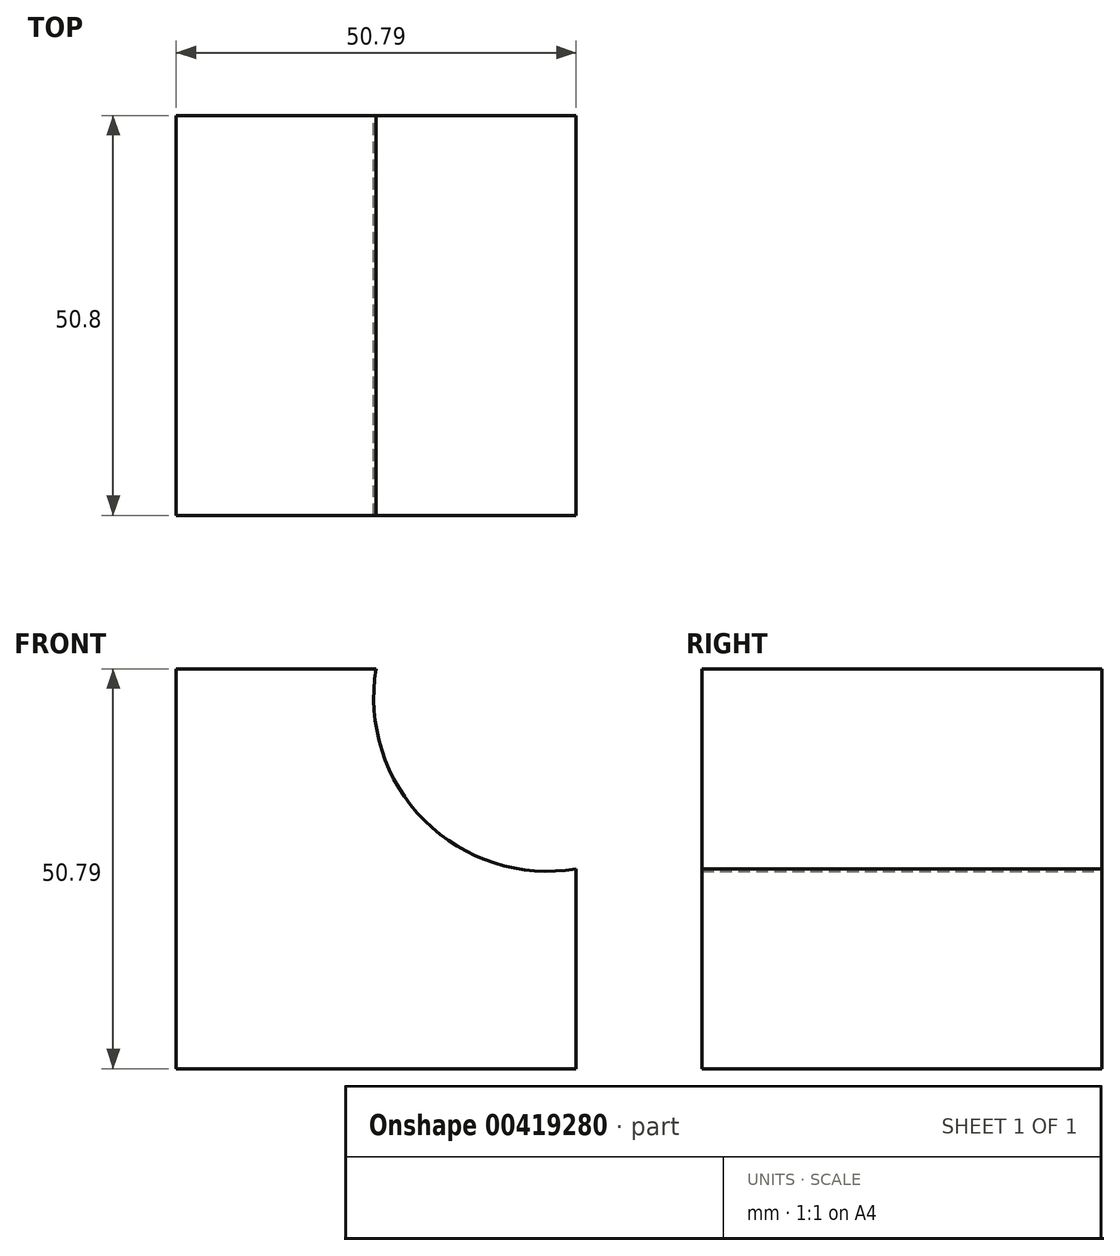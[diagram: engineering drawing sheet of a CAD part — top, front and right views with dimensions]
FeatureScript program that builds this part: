
annotation { "Feature Type Name" : "Feature", "Feature Type Description" : "" }
export const myFeature = defineFeature(function(context is Context, id is Id, definition is map)
    precondition{}
    {
        {
            var Q0;
            Q0=qCreatedBy(makeId("Front.planeOp"),FACE);
            var sketch = newSketch(context, id + "F0", { "sketchPlane" : qUnion([Q0])});
            skLineSegment(sketch, "E0", {"start": v(0, 0) * mm, "end": v(0, 50.8) * mm});
            skLineSegment(sketch, "E1", {"start": v(0, 50.8) * mm, "end": v(25.4, 50.8) * mm});
            skLineSegment(sketch, "E2", {"start": v(0, 0) * mm, "end": v(50.8, 0) * mm});
            skLineSegment(sketch, "E3", {"start": v(50.8, 0) * mm, "end": v(50.8, 25.4) * mm});
            skArc(sketch, "E4", {"start": v(25.4, 50.8) * mm, "mid": v(31.53, 31.53) * mm, "end": v(50.8, 25.4) * mm});
            skSolve(sketch);
        }
        {
            var Q0;
            Q0=makeQuery(id+"F0.imprint","IMPRINT",FACE,{"disambiguationData":[TD([[makeQuery(id+"F0.imprint","IMPRINT",EDGE,{"derivedFrom":sQuery(id+"F0.wireOp",EDGE,"E0")}),-1.0]])]});
            extrude(context, id + "F1", {"entities" : qUnion([Q0]), "depth" : 50.8 * mm});
        }
    });
